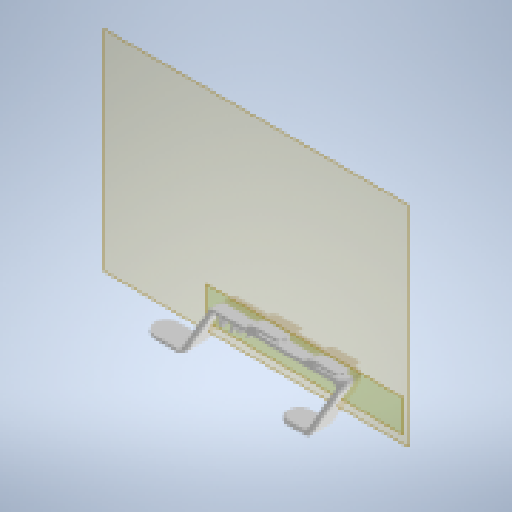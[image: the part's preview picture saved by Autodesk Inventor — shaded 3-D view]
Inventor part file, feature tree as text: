
AUTODESK INVENTOR PART (.ipt)
format: ipt  version: 2024.1 (Build 281209000, 209)  size: 887,808 bytes
history: native  units: mm
features: fillet x10, chamfer x6, other x4, extrude x3, projected_geometry x3, plane x2, sketch x1, reference x1
ambient origin geometry x8: Origin, YZ Plane, XZ Plane, XY Plane, X Axis, Y Axis, Z Axis, Center Point
bodies: Body1 (feature_tree)
feature tree (30):
  other  "cable-hanger"
  extrude  "Extrusion1"  Depth=3.0mm
  fillet  "Fillet1"  Radius=10.0mm
  fillet  "Fillet2"  Radius=1.0mm
  chamfer  "Chamfer8"  Distance=6.0mm
  fillet  "Fillet8"  Radius=8.0mm
  fillet  "Fillet17"  Radius=1.2mm
  chamfer  "Chamfer1"  Distance=1.4mm
  plane  "Work Plane1"
  extrude  "Extrusion2"  Depth=3.0mm
  fillet  "Fillet3"  Radius=1.5mm
  fillet  "Fillet4"  Radius=4.0mm
  chamfer  "Chamfer2"  Distance=2.0mm
  plane  "Work Plane2"
  fillet  "Fillet9"  Radius=8.0mm
  extrude  "Extrusion3"  Depth=3.0mm
  chamfer  "Chamfer3"  Distance=1.0mm
  chamfer  "Chamfer4"  Distance=1.0mm Angle=45.0deg
  fillet  "Fillet10"  Radius=3.0mm
  chamfer  "Chamfer5"  Distance=8.0mm
  fillet  "Fillet12"  Radius=0.8mm
  fillet  "Fillet13"  Radius=0.5mm
  sketch  "Sketch2"  dims[d14=15.0mm d15=0.0mm d16=7.5mm d17=10.0mm d18=1.0mm d19=2.0mm d20=45.0deg d54=6.0mm d55=8.0mm d60=1.2mm d61=1.2mm d62=1.4mm d65=3.0mm d66=1.5mm d67=4.0mm d68=2.0mm d69=8.0mm d70=0.0mm d71=1.0mm d72=1.0mm d73=1.0mm d74=2.0mm d75=45.0deg d76=3.0mm d78=8.0mm d79=0.0mm d80=0.8mm d81=2.0mm d82=45.0deg d83=0.5mm d84=2.0mm d85=45.0deg d96=0.5mm d97=2.0mm d98=45.0deg d131=3.0mm d132=2.0mm d133=45.0deg d134=2.0mm d136=6.0mm d137=5.0mm d138=11.0mm d139=4.0mm d140=13.0mm d143=0.7mm d145=0.7mm d153=13.0mm d154=3.0mm d159=12.011689mm d160=7.0mm d161=15.0mm d162=37.0mm d163=7.0mm d164=15.0mm d165=1.5mm d166=2.0mm d167=3.0mm d168=2.8mm d169=35.0mm d170=3.0mm d171=15.0mm d172=25.0mm d173=3.0mm d174=60.0deg d175=3.0mm d176=20.0mm d178=60.0deg d179=60.0deg d181=3.0mm d182=30.0mm d184=80.0mm d189=6.5mm d190=5.803848mm]
  projected_geometry  "Projected Loop2"
  projected_geometry  "Projected Loop3"
  projected_geometry  "Projected Loop4"
  reference  "Reference3"
  other  "<userpath>\Documents\0004-CAD\3D-cad-main\cable-hanger\VERSION3-largel-upright-hook.iam"
  other  "VERSION3-largel-upright-hook.iam"
  other  "backplate-0:1"
